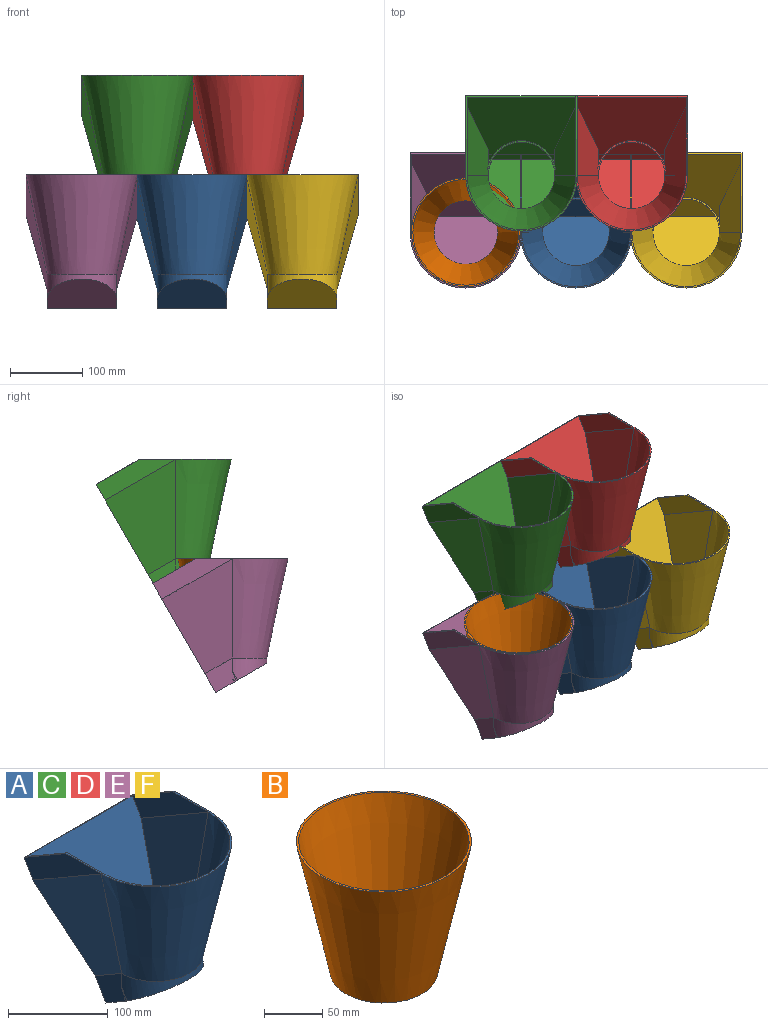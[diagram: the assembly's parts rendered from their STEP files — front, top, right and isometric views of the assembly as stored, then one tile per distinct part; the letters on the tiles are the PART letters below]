
ASSEMBLY  parts=6 mates=1
PART A: 31 faces, bbox 154.5x187x185.2 mm
  f0: plane 154x150.38mm, normal (0,0.87,-0.5), area 21539.2mm2, adj f1,f2,f4,f5,f15,f23,f25,f26
  f1: plane 109.46x55.98mm, normal (-1,0,0), area 2257.9mm2, adj f0,f15,f20,f23
  f2: plane 109.46x55.98mm, normal (1,0,0), area 2257.9mm2, adj f0,f15,f20,f25
  f3: cylinder r=47.88mm len=95.76mm, axis (0,0,1), area 2433.2mm2, adj f4,f5,f21,f26,f29,f30
  f4: plane 47.71x43.08mm, normal (1,0,0), area 1090.9mm2, adj f0,f3,f5,f25,f30
  f5: plane 95.8x70.56mm, normal (0,-0.5,-0.87), area 6664.2mm2, adj f0,f3,f4,f26,f29,f30
  f6: plane 34.62x12.63mm, normal (0,0,-1), area 51mm2, adj f8,f12,f13,f14,f27,f28
  f7: cylinder r=47.88mm len=47mm, axis (0,0,1), area 1028mm2, adj f9,f11,f18,f24,f28
  f8: cylinder r=45.88mm len=91.76mm, axis (0,0,1), area 5194.2mm2, adj f6,f9,f18,f19,f27,f28
  f9: plane 34.62x12.63mm, normal (0,0,-1), area 51mm2, adj f7,f8,f10,f11,f27,f28
  f10: extruded ~4.98x4.31mm, area 5.5mm2, adj f9,f11,f27
  f11: plane 37.08x36.22mm, normal (-1,0,0), area 577.4mm2, adj f7,f9,f10,f24,f27,f28
  f12: plane 37.08x36.22mm, normal (1,0,0), area 577.4mm2, adj f6,f13,f14,f22,f27,f28
  f13: extruded ~4.98x4.31mm, area 5.5mm2, adj f6,f12,f27
  f14: cylinder r=47.88mm len=47mm, axis (0,0,1), area 1028mm2, adj f6,f12,f18,f22,f28
  f15: plane 154x59.46mm, normal (0,0.5,0.87), area 574.7mm2, adj f0,f1,f2,f16,f17,f20,f28
  f16: plane 107.73x54.98mm, normal (1,0,0), area 2207.9mm2, adj f15,f20,f22,f28
  f17: plane 107.73x54.98mm, normal (-1,0,0), area 2207.9mm2, adj f15,f20,f24,f28
  f18: plane 94x47.88mm, normal (0,0,1), area 273.6mm2, adj f7,f8,f14,f22,f24
  f19: cone r=75mm half-angle=12deg, axis (0,0,1), area 26594.4mm2, adj f8,f20,f22,f24
  f20: plane 154x127mm, normal (0,0,1), area 677.5mm2, adj f1,f2,f15,f16,f17,f19,f21
  f21: cone r=77mm half-angle=12deg, axis (0,0,1), area 27474.4mm2, adj f3,f20,f23,f25
  f22: plane 158.24x95.74mm, normal (0.97,0.12,0.21), area 9211.8mm2, adj f12,f14,f16,f18,f19,f28
  f23: plane 158.73x96.96mm, normal (-0.97,-0.12,-0.21), area 9494.2mm2, adj f0,f1,f21,f26
  f24: plane 158.24x95.74mm, normal (-0.97,0.12,0.21), area 9211.8mm2, adj f7,f11,f17,f18,f19,f28
  f25: plane 158.73x96.96mm, normal (0.97,-0.12,-0.21), area 9494.2mm2, adj f0,f2,f4,f21
  f26: plane 47.71x43.08mm, normal (-1,0,0), area 1090.9mm2, adj f0,f3,f5,f23,f29
  f27: plane 93.66x67.79mm, normal (0,0.5,0.87), area 6144.3mm2, adj f6,f8,f9,f10,f11,f12,f13,f28
  f28: plane 150x148.65mm, normal (0,-0.87,0.5), area 20338.3mm2, adj f6,f7,f8,f9,f11,f12,f14,f15
  f29: bspline ~16.95x9.18mm, area 18.5mm2, adj f3,f5,f26
  f30: bspline ~16.95x9.18mm, area 18.5mm2, adj f3,f4,f5
PART B: 4 faces, bbox 150x150x137 mm
  f0: cone r=73mm half-angle=12deg, axis (0,0,1), area 51428.7mm2, adj f1,f3
  f1: plane 150x150mm, normal (0,0,1), area 929.9mm2, adj f0,f2
  f2: cone r=75mm half-angle=12deg, axis (0,0,1), area 53188.7mm2, adj f1,f3
  f3: plane 91.76x91.76mm, normal (0,0,-1), area 564mm2, adj f0,f2
PART C: same geometry as A
PART D: same geometry as A
PART E: same geometry as A
PART F: same geometry as A
PLACE A t=(125.09,-15.34,-45.44)mm fixed
PLACE B t=(-26.91,-15.34,-45.44)mm
PLACE C rot(axis=(0,-0.87,0.5),0deg) t=(49.91,63.03,91.52)mm
PLACE D rot(axis=(0,-0.87,0.5),0deg) t=(201.91,63.03,91.52)mm
PLACE E t=(-26.91,-15.34,-45.44)mm fixed
PLACE F t=(277.09,-15.34,-45.44)mm fixed
MATE planar B.f0 <-> E.f19  axis (0,0,1) through (-26.91,-15.34,23.06)mm
